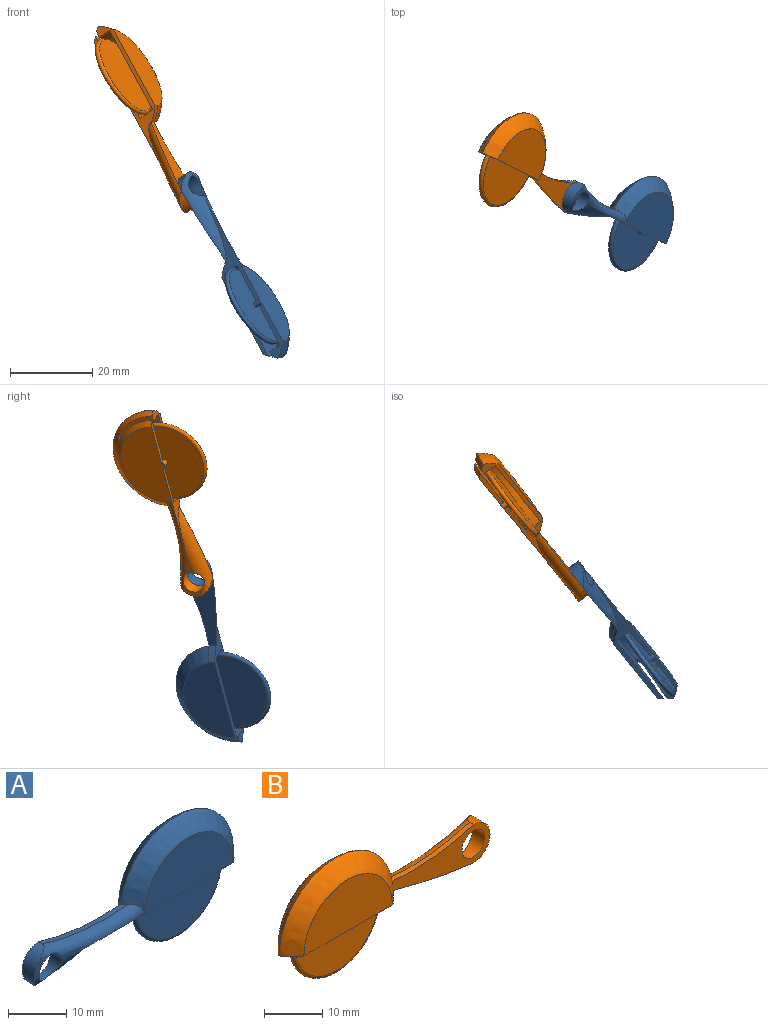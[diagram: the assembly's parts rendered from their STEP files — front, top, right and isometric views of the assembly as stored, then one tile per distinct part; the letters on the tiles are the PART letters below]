
ASSEMBLY  parts=2 mates=1
PART A: 25 faces, bbox 52.9x7x26.3 mm
  f0: plane 2.67x2.6mm, normal (0,-1,0), area 3.5mm2, adj f4,f6,f23,f24
  f1: plane 0.82x0.3mm, normal (0,-1,0), area 0.1mm2, adj f6,f23,f24
  f2: plane 41.91x7.02mm, normal (0,0,-1), area 58mm2, adj f7,f8,f9,f10,f11,f16,f17,f21
  f3: plane 14.57x5.22mm, normal (0,0,-1), area 17.5mm2, adj f7,f10,f11,f13,f17,f18,f22
  f4: cylinder r=4.02mm len=8.03mm, axis (0,1,0), area 26.3mm2, adj f0,f5,f15,f23,f24
  f5: cylinder r=49.51mm len=20.58mm, axis (0,1,0), area 20.5mm2, adj f4,f15,f18,f23
  f6: cylinder r=2.76mm len=5.52mm, axis (0,1,0), area 45.4mm2, adj f0,f1,f15,f23,f24
  f7: cylinder r=11.28mm len=22.56mm, axis (0,1,0), area 130.7mm2, adj f2,f3,f8,f10,f12,f13,f14,f21
  f8: plane 23.3x11.3mm, normal (0,-1,0), area 208.9mm2, adj f2,f7,f12,f17
  f9: plane 21.42x10.79mm, normal (0,1,0), area 180.1mm2, adj f2,f16,f17
  f10: plane 22.56x11.28mm, normal (0,1,0), area 198.9mm2, adj f2,f3,f7,f22
  f11: plane 23.8x11.54mm, normal (0,-1,0), area 181.3mm2, adj f2,f3,f18,f22,f23
  f12: cylinder r=10.71mm len=1.28mm, axis (0,1,0), area 0.2mm2, adj f7,f8,f14,f17
  f13: plane 10.12x7.1mm, normal (0,1,0), area 17.8mm2, adj f3,f7,f14,f17
  f14: torus R=10.11mm, axis (0,-1,0), area 1.7mm2, adj f7,f12,f13,f17
  f15: plane 23.85x8.03mm, normal (0,1,0), area 92.3mm2, adj f4,f5,f6,f16,f24
  f16: bspline ~3.14x3mm, area 7.5mm2, adj f2,f9,f15,f17
  f17: bspline ~27.28x13.71mm, area 144.7mm2, adj f2,f3,f8,f9,f12,f13,f14,f16
  f18: bspline ~27.41x13.71mm, area 158.4mm2, adj f3,f5,f11,f17,f23
  f19: plane 20.23x20.23mm, normal (0,-1,0), area 319.5mm2, adj f21,f22
  f20: plane 20.23x20.23mm, normal (0,1,0), area 321.3mm2, adj f21
  f21: torus R=10.11mm, axis (0,-1,0), area 125mm2, adj f2,f7,f19,f20
  f22: cylinder r=0.76mm len=1.8mm, axis (0,1,0), area 6.2mm2, adj f2,f3,f10,f11,f19
  f23: torus R=51.51mm, axis (0,-1,0), area 70.5mm2, adj f0,f1,f2,f4,f5,f6,f11,f18
  f24: torus R=112.12mm, axis (0,1,0), area 68.9mm2, adj f0,f1,f2,f4,f6,f15,f23
PART B: 25 faces, bbox 52.9x7x26.3 mm
  f0: plane 7.04x1.89mm, normal (0,1,0), area 4.8mm2, adj f2,f6,f23,f24
  f1: plane 4.24x2.6mm, normal (0,1,0), area 5.5mm2, adj f4,f6,f23,f24
  f2: plane 41.45x7.02mm, normal (0,0,-1), area 59.2mm2, adj f0,f7,f8,f9,f10,f11,f13,f16
  f3: plane 11.57x1mm, normal (0,0,-1), area 11mm2, adj f8,f9,f16,f22
  f4: cylinder r=4.02mm len=8.03mm, axis (0,1,0), area 31.2mm2, adj f1,f5,f15,f23,f24
  f5: cylinder r=49.51mm len=20.58mm, axis (0,1,0), area 20.5mm2, adj f4,f15,f16,f24
  f6: cylinder r=2.76mm len=5.52mm, axis (0,1,0), area 52mm2, adj f0,f1,f15,f23,f24
  f7: cylinder r=11.28mm len=22.56mm, axis (0,1,0), area 131.8mm2, adj f2,f8,f10,f12,f13,f14
  f8: plane 23.3x11.3mm, normal (0,-1,0), area 208mm2, adj f2,f3,f7,f12,f16,f22
  f9: plane 23.8x11.51mm, normal (0,1,0), area 181.3mm2, adj f2,f3,f16,f22,f24
  f10: plane 22.56x11.28mm, normal (0,1,0), area 199.8mm2, adj f2,f7
  f11: plane 21.42x10.79mm, normal (0,-1,0), area 180.1mm2, adj f2,f17,f18
  f12: cylinder r=10.71mm len=1.28mm, axis (0,1,0), area 0.2mm2, adj f7,f8,f14,f16
  f13: plane 10.12x7.1mm, normal (0,1,0), area 17.8mm2, adj f2,f7,f14,f16
  f14: torus R=10.11mm, axis (0,-1,0), area 1.7mm2, adj f7,f12,f13,f16
  f15: plane 23.85x8.03mm, normal (0,-1,0), area 92.3mm2, adj f4,f5,f6,f18,f23
  f16: bspline ~27.41x13.71mm, area 144.6mm2, adj f2,f3,f5,f8,f9,f12,f13,f14
  f17: bspline ~27.28x13.71mm, area 158.5mm2, adj f2,f11,f16,f18
  f18: bspline ~3.13x3mm, area 7.5mm2, adj f2,f11,f15,f17
  f19: plane 20.23x20.23mm, normal (0,-1,0), area 321.3mm2, adj f21
  f20: plane 20.23x20.23mm, normal (0,1,0), area 319.7mm2, adj f21,f22
  f21: torus R=10.11mm, axis (0,-1,0), area 124.3mm2, adj f19,f20
  f22: cylinder r=0.72mm len=1.8mm, axis (0,-1,0), area 5.9mm2, adj f2,f3,f8,f9,f20
  f23: torus R=113.7mm, axis (0,1,0), area 75.6mm2, adj f0,f1,f2,f4,f6,f15
  f24: torus R=51.51mm, axis (0,1,0), area 68.3mm2, adj f0,f1,f2,f4,f5,f6,f9,f16
PLACE A rot(axis=(-0.72,0.64,0.28),96.1deg) t=(-39.23,16.32,-12.72)mm
PLACE B rot(axis=(-0.72,0.64,0.28),96.1deg) t=(-39.23,16.32,-12.72)mm
MATE pin_slot A.f6 <-> B.f4  axis (-0.78,0.34,-0.52) through (-37.66,15.64,-11.69)mm
